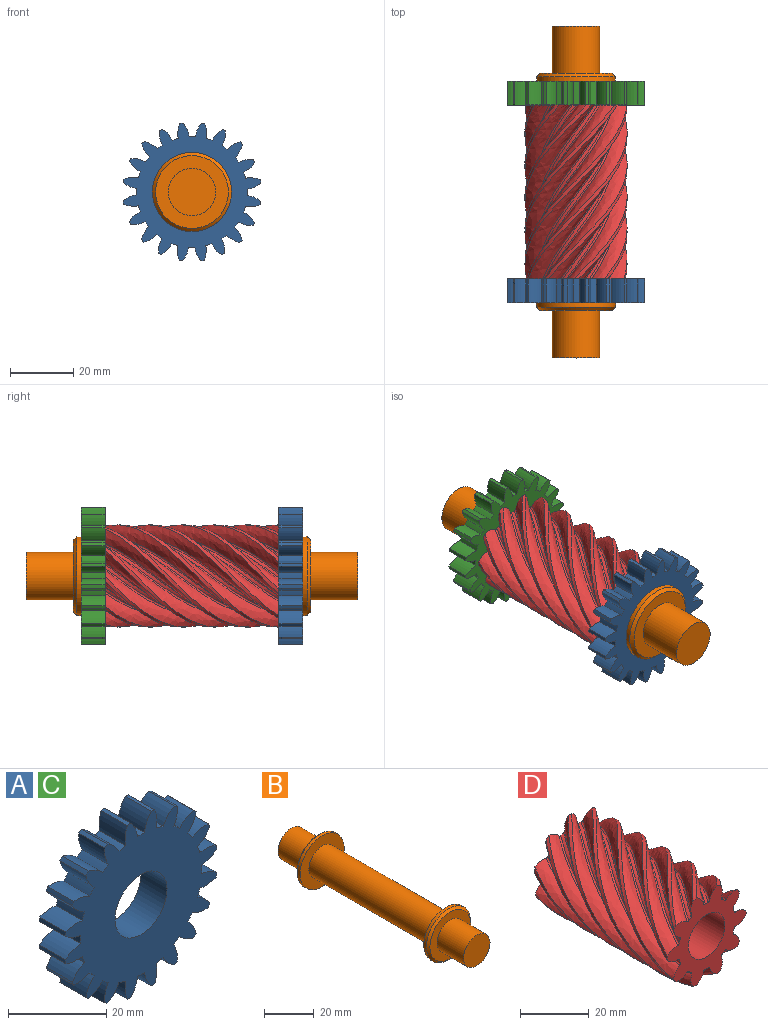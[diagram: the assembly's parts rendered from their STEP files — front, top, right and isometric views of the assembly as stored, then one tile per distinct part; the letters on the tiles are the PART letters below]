
ASSEMBLY  parts=4 mates=3
PART A: 83 faces, bbox 43.6x7.5x43.6 mm
  f0: cylinder r=22mm len=7.5mm, axis (0,-1,0), area 7.8mm2, adj f2,f76,f79,f80
  f1: cylinder r=8mm len=7.5mm, axis (0,-1,0), area 36.1mm2, adj f3,f4,f76,f79
  f2: cylinder r=8mm len=7.5mm, axis (0,-1,0), area 36.1mm2, adj f0,f3,f76,f79
  f3: cylinder r=17.5mm len=7.5mm, axis (0,-1,0), area 15mm2, adj f1,f2,f76,f79
  f4: cylinder r=22mm len=7.5mm, axis (0,-1,0), area 7.8mm2, adj f1,f6,f76,f79
  f5: cylinder r=8mm len=7.5mm, axis (0,-1,0), area 36.1mm2, adj f7,f8,f76,f79
  f6: cylinder r=8mm len=7.5mm, axis (0,-1,0), area 36.1mm2, adj f4,f7,f76,f79
  f7: cylinder r=17.5mm len=7.5mm, axis (0,-1,0), area 15mm2, adj f5,f6,f76,f79
  f8: cylinder r=22mm len=7.5mm, axis (0,-1,0), area 7.8mm2, adj f5,f10,f76,f79
  f9: cylinder r=8mm len=7.5mm, axis (0,-1,0), area 36.1mm2, adj f11,f12,f76,f79
  f10: cylinder r=8mm len=7.5mm, axis (0,-1,0), area 36.1mm2, adj f8,f11,f76,f79
  f11: cylinder r=17.5mm len=7.5mm, axis (0,-1,0), area 15mm2, adj f9,f10,f76,f79
  f12: cylinder r=22mm len=7.5mm, axis (0,-1,0), area 7.8mm2, adj f9,f14,f76,f79
  f13: cylinder r=8mm len=7.5mm, axis (0,-1,0), area 36.1mm2, adj f15,f16,f76,f79
  f14: cylinder r=8mm len=7.5mm, axis (0,-1,0), area 36.1mm2, adj f12,f15,f76,f79
  f15: cylinder r=17.5mm len=7.5mm, axis (0,-1,0), area 15mm2, adj f13,f14,f76,f79
  f16: cylinder r=22mm len=7.5mm, axis (0,-1,0), area 7.8mm2, adj f13,f18,f76,f79
  f17: cylinder r=8mm len=7.5mm, axis (0,-1,0), area 36.1mm2, adj f19,f20,f76,f79
  f18: cylinder r=8mm len=7.5mm, axis (0,-1,0), area 36.1mm2, adj f16,f19,f76,f79
  f19: cylinder r=17.5mm len=7.5mm, axis (0,-1,0), area 15mm2, adj f17,f18,f76,f79
  f20: cylinder r=22mm len=7.5mm, axis (0,-1,0), area 7.8mm2, adj f17,f22,f76,f79
  f21: cylinder r=8mm len=7.5mm, axis (0,-1,0), area 36.1mm2, adj f23,f24,f76,f79
  f22: cylinder r=8mm len=7.5mm, axis (0,-1,0), area 36.1mm2, adj f20,f23,f76,f79
  f23: cylinder r=17.5mm len=7.5mm, axis (0,-1,0), area 15mm2, adj f21,f22,f76,f79
  f24: cylinder r=22mm len=7.5mm, axis (0,-1,0), area 7.8mm2, adj f21,f26,f76,f79
  f25: cylinder r=8mm len=7.5mm, axis (0,-1,0), area 36.1mm2, adj f27,f28,f76,f79
  f26: cylinder r=8mm len=7.5mm, axis (0,-1,0), area 36.1mm2, adj f24,f27,f76,f79
  f27: cylinder r=17.5mm len=7.5mm, axis (0,-1,0), area 15mm2, adj f25,f26,f76,f79
  f28: cylinder r=22mm len=7.5mm, axis (0,-1,0), area 7.8mm2, adj f25,f30,f76,f79
  f29: cylinder r=8mm len=7.5mm, axis (0,-1,0), area 36.1mm2, adj f31,f32,f76,f79
  f30: cylinder r=8mm len=7.5mm, axis (0,-1,0), area 36.1mm2, adj f28,f31,f76,f79
  f31: cylinder r=17.5mm len=7.5mm, axis (0,-1,0), area 15mm2, adj f29,f30,f76,f79
  f32: cylinder r=22mm len=7.5mm, axis (0,-1,0), area 7.8mm2, adj f29,f34,f76,f79
  f33: cylinder r=8mm len=7.5mm, axis (0,-1,0), area 36.1mm2, adj f35,f36,f76,f79
  f34: cylinder r=8mm len=7.5mm, axis (0,-1,0), area 36.1mm2, adj f32,f35,f76,f79
  f35: cylinder r=17.5mm len=7.5mm, axis (0,-1,0), area 15mm2, adj f33,f34,f76,f79
  f36: cylinder r=22mm len=7.5mm, axis (0,-1,0), area 7.8mm2, adj f33,f38,f76,f79
  f37: cylinder r=8mm len=7.5mm, axis (0,-1,0), area 36.1mm2, adj f39,f40,f76,f79
  f38: cylinder r=8mm len=7.5mm, axis (0,-1,0), area 36.1mm2, adj f36,f39,f76,f79
  f39: cylinder r=17.5mm len=7.5mm, axis (0,-1,0), area 15mm2, adj f37,f38,f76,f79
  f40: cylinder r=22mm len=7.5mm, axis (0,-1,0), area 7.8mm2, adj f37,f42,f76,f79
  f41: cylinder r=8mm len=7.5mm, axis (0,-1,0), area 36.1mm2, adj f43,f44,f76,f79
  f42: cylinder r=8mm len=7.5mm, axis (0,-1,0), area 36.1mm2, adj f40,f43,f76,f79
  f43: cylinder r=17.5mm len=7.5mm, axis (0,-1,0), area 15mm2, adj f41,f42,f76,f79
  f44: cylinder r=22mm len=7.5mm, axis (0,-1,0), area 7.8mm2, adj f41,f46,f76,f79
  f45: cylinder r=8mm len=7.5mm, axis (0,-1,0), area 36.1mm2, adj f47,f48,f76,f79
  f46: cylinder r=8mm len=7.5mm, axis (0,-1,0), area 36.1mm2, adj f44,f47,f76,f79
  f47: cylinder r=17.5mm len=7.5mm, axis (0,-1,0), area 15mm2, adj f45,f46,f76,f79
  f48: cylinder r=22mm len=7.5mm, axis (0,-1,0), area 7.8mm2, adj f45,f50,f76,f79
  f49: cylinder r=8mm len=7.5mm, axis (0,-1,0), area 36.1mm2, adj f51,f52,f76,f79
  f50: cylinder r=8mm len=7.5mm, axis (0,-1,0), area 36.1mm2, adj f48,f51,f76,f79
  f51: cylinder r=17.5mm len=7.5mm, axis (0,-1,0), area 15mm2, adj f49,f50,f76,f79
  f52: cylinder r=22mm len=7.5mm, axis (0,-1,0), area 7.8mm2, adj f49,f54,f76,f79
  f53: cylinder r=8mm len=7.5mm, axis (0,-1,0), area 36.1mm2, adj f55,f56,f76,f79
  f54: cylinder r=8mm len=7.5mm, axis (0,-1,0), area 36.1mm2, adj f52,f55,f76,f79
  f55: cylinder r=17.5mm len=7.5mm, axis (0,-1,0), area 15mm2, adj f53,f54,f76,f79
  f56: cylinder r=22mm len=7.5mm, axis (0,-1,0), area 7.8mm2, adj f53,f58,f76,f79
  f57: cylinder r=8mm len=7.5mm, axis (0,-1,0), area 36.1mm2, adj f59,f60,f76,f79
  f58: cylinder r=8mm len=7.5mm, axis (0,-1,0), area 36.1mm2, adj f56,f59,f76,f79
  f59: cylinder r=17.5mm len=7.5mm, axis (0,-1,0), area 15mm2, adj f57,f58,f76,f79
  f60: cylinder r=22mm len=7.5mm, axis (0,-1,0), area 7.8mm2, adj f57,f62,f76,f79
  f61: cylinder r=8mm len=7.5mm, axis (0,-1,0), area 36.1mm2, adj f63,f64,f76,f79
  f62: cylinder r=8mm len=7.5mm, axis (0,-1,0), area 36.1mm2, adj f60,f63,f76,f79
  f63: cylinder r=17.5mm len=7.5mm, axis (0,-1,0), area 15mm2, adj f61,f62,f76,f79
  f64: cylinder r=22mm len=7.5mm, axis (0,-1,0), area 7.8mm2, adj f61,f66,f76,f79
  f65: cylinder r=8mm len=7.5mm, axis (0,-1,0), area 36.1mm2, adj f67,f68,f76,f79
  f66: cylinder r=8mm len=7.5mm, axis (0,-1,0), area 36.1mm2, adj f64,f67,f76,f79
  f67: cylinder r=17.5mm len=7.5mm, axis (0,-1,0), area 15mm2, adj f65,f66,f76,f79
  f68: cylinder r=22mm len=7.5mm, axis (0,-1,0), area 7.8mm2, adj f65,f70,f76,f79
  f69: cylinder r=8mm len=7.5mm, axis (0,-1,0), area 36.1mm2, adj f71,f72,f76,f79
  f70: cylinder r=8mm len=7.5mm, axis (0,-1,0), area 36.1mm2, adj f68,f71,f76,f79
  f71: cylinder r=17.5mm len=7.5mm, axis (0,-1,0), area 15mm2, adj f69,f70,f76,f79
  f72: cylinder r=22mm len=7.5mm, axis (0,-1,0), area 7.8mm2, adj f69,f74,f76,f79
  f73: cylinder r=8mm len=7.5mm, axis (0,-1,0), area 36.1mm2, adj f75,f76,f78,f79
  f74: cylinder r=8mm len=7.5mm, axis (0,-1,0), area 36.1mm2, adj f72,f75,f76,f79
  f75: cylinder r=17.5mm len=7.5mm, axis (0,-1,0), area 15mm2, adj f73,f74,f76,f79
  f76: plane 43.61x43.61mm, normal (0,-1,0), area 1034.8mm2, adj f0,f1,f2,f3,f4,f5,f6,f7
  f77: cylinder r=7.5mm len=15mm, axis (0,-1,0), area 353.4mm2, adj f76,f79
  f78: cylinder r=22mm len=7.5mm, axis (0,-1,0), area 7.8mm2, adj f73,f76,f79,f81
  f79: plane 43.61x43.61mm, normal (0,1,0), area 1034.8mm2, adj f0,f1,f2,f3,f4,f5,f6,f7
  f80: cylinder r=8mm len=7.5mm, axis (0,-1,0), area 36.1mm2, adj f0,f76,f79,f82
  f81: cylinder r=8mm len=7.5mm, axis (0,-1,0), area 36.1mm2, adj f76,f78,f79,f82
  f82: cylinder r=17.5mm len=7.5mm, axis (0,-1,0), area 15mm2, adj f76,f79,f80,f81
PART B: 13 faces, bbox 25x105x25 mm
  f0: plane 15x15mm, normal (0,1,0), area 176.7mm2, adj f10
  f1: plane 15x15mm, normal (0,-1,0), area 176.7mm2, adj f2
  f2: cylinder r=7.5mm len=15mm, axis (0,-1,0), area 706.9mm2, adj f1,f3
  f3: plane 23x23mm, normal (0,-1,0), area 238.8mm2, adj f2,f12
  f4: cylinder r=12.5mm len=25mm, axis (0,-1,0), area 117.8mm2, adj f5,f12
  f5: plane 25x25mm, normal (0,1,0), area 314.2mm2, adj f4,f6
  f6: cylinder r=7.5mm len=70mm, axis (0,-1,0), area 3298.7mm2, adj f5,f7
  f7: plane 25x25mm, normal (0,-1,0), area 314.2mm2, adj f6,f8
  f8: cylinder r=12.5mm len=25mm, axis (0,-1,0), area 117.8mm2, adj f7,f11
  f9: plane 23x23mm, normal (0,1,0), area 238.8mm2, adj f10,f11
  f10: cylinder r=7.5mm len=15mm, axis (0,-1,0), area 706.9mm2, adj f0,f9
  f11: cone r=12.5mm half-angle=45deg, axis (0,-1,0), area 106.6mm2, adj f8,f9
  f12: cone r=11.5mm half-angle=45deg, axis (0,1,0), area 106.6mm2, adj f3,f4
PART C: same geometry as A
PART D: 63 faces, bbox 33.1x59.2x33.1 mm
  f0: cylinder r=11.65mm len=55mm, axis (0,-1,0), area 68.8mm2, adj f11,f12,f44,f62
  f1: cylinder r=11.65mm len=55mm, axis (0,-1,0), area 68.8mm2, adj f11,f12,f43,f46
  f2: cylinder r=11.65mm len=55mm, axis (0,-1,0), area 68.8mm2, adj f11,f12,f45,f48
  f3: cylinder r=11.65mm len=55mm, axis (0,-1,0), area 68.8mm2, adj f11,f12,f47,f50
  f4: cylinder r=11.65mm len=55mm, axis (0,-1,0), area 68.8mm2, adj f11,f12,f49,f52
  f5: cylinder r=11.65mm len=55mm, axis (0,-1,0), area 68.8mm2, adj f11,f12,f53,f56
  f6: cylinder r=11.65mm len=55mm, axis (0,-1,0), area 68.8mm2, adj f11,f12,f55,f58
  f7: cylinder r=11.65mm len=55mm, axis (0,-1,0), area 68.8mm2, adj f11,f12,f51,f54
  f8: cylinder r=11.65mm len=55mm, axis (0,-1,0), area 68.8mm2, adj f11,f12,f57,f60
  f9: cylinder r=11.65mm len=55mm, axis (0,-1,0), area 68.8mm2, adj f11,f12,f59,f61
  f10: cylinder r=7.5mm len=55mm, axis (0,-1,0), area 2591.8mm2, adj f11,f12
  f11: plane 32.41x31.74mm, normal (0,1,0), area 440.6mm2, adj f0,f1,f2,f3,f4,f5,f6,f7
  f12: plane 32.42x31.27mm, normal (0,-1,0), area 440.6mm2, adj f0,f1,f2,f3,f4,f5,f6,f7
  f13: bspline ~57.29x32.56mm, area 82.5mm2, adj f11,f12,f14,f15
  f14: bspline ~57.29x32.41mm, area 329.3mm2, adj f11,f12,f13,f62
  f15: bspline ~57.29x32.56mm, area 329.3mm2, adj f11,f12,f13,f61
  f16: bspline ~57.29x32.33mm, area 82.5mm2, adj f11,f12,f17,f18
  f17: bspline ~55x31.42mm, area 329.3mm2, adj f11,f12,f16,f59
  f18: bspline ~57.29x31.92mm, area 329.3mm2, adj f11,f12,f16,f60
  f19: bspline ~57.29x30.62mm, area 82.5mm2, adj f11,f12,f20,f21
  f20: bspline ~57.29x30.55mm, area 329.3mm2, adj f11,f12,f19,f53
  f21: bspline ~57.29x29.96mm, area 329.3mm2, adj f11,f12,f19,f54
  f22: bspline ~57.29x32mm, area 82.5mm2, adj f11,f12,f23,f24
  f23: bspline ~57.29x31.36mm, area 329.3mm2, adj f11,f12,f22,f57
  f24: bspline ~57.29x32mm, area 329.3mm2, adj f11,f12,f22,f58
  f25: bspline ~55x32.3mm, area 82.5mm2, adj f11,f12,f26,f27
  f26: bspline ~57.29x32.85mm, area 329.3mm2, adj f11,f12,f25,f55
  f27: bspline ~55x32.2mm, area 329.3mm2, adj f11,f12,f25,f56
  f28: bspline ~57.29x32.56mm, area 82.5mm2, adj f11,f12,f29,f30
  f29: bspline ~57.29x32.41mm, area 329.3mm2, adj f11,f12,f28,f51
  f30: bspline ~57.29x32.56mm, area 329.3mm2, adj f11,f12,f28,f52
  f31: bspline ~57.29x32.33mm, area 82.5mm2, adj f11,f12,f32,f33
  f32: bspline ~55x31.42mm, area 329.3mm2, adj f11,f12,f31,f49
  f33: bspline ~57.29x31.92mm, area 329.3mm2, adj f11,f12,f31,f50
  f34: bspline ~57.29x32mm, area 82.5mm2, adj f11,f12,f35,f36
  f35: bspline ~57.29x31.36mm, area 329.3mm2, adj f11,f12,f34,f47
  f36: bspline ~57.29x32mm, area 329.3mm2, adj f11,f12,f34,f48
  f37: bspline ~55x32.3mm, area 82.5mm2, adj f11,f12,f38,f39
  f38: bspline ~57.29x32.85mm, area 329.3mm2, adj f11,f12,f37,f45
  f39: bspline ~55x32.2mm, area 329.3mm2, adj f11,f12,f37,f46
  f40: bspline ~57.29x30.62mm, area 82.5mm2, adj f11,f12,f41,f42
  f41: bspline ~57.29x30.55mm, area 329.3mm2, adj f11,f12,f40,f43
  f42: bspline ~57.29x29.96mm, area 329.3mm2, adj f11,f12,f40,f44
  f43: bspline ~58.6x23.38mm, area 49.4mm2, adj f1,f11,f12,f41
  f44: bspline ~57.55x23.56mm, area 49.4mm2, adj f0,f11,f12,f42
  f45: bspline ~58.6x24.21mm, area 49.4mm2, adj f2,f11,f12,f38
  f46: bspline ~57.55x23.9mm, area 49.4mm2, adj f1,f11,f12,f39
  f47: bspline ~58.6x23.11mm, area 49.4mm2, adj f3,f11,f12,f35
  f48: bspline ~57.55x24.21mm, area 49.4mm2, adj f2,f11,f12,f36
  f49: bspline ~58.6x24.18mm, area 49.4mm2, adj f4,f11,f12,f32
  f50: bspline ~57.55x22.48mm, area 49.4mm2, adj f3,f11,f12,f33
  f51: bspline ~58.6x24.12mm, area 49.4mm2, adj f7,f11,f12,f29
  f52: bspline ~57.55x24.21mm, area 49.4mm2, adj f4,f11,f12,f30
  f53: bspline ~58.6x23.38mm, area 49.4mm2, adj f5,f11,f12,f20
  f54: bspline ~57.55x23.56mm, area 49.4mm2, adj f7,f11,f12,f21
  f55: bspline ~58.6x24.21mm, area 49.4mm2, adj f6,f11,f12,f26
  f56: bspline ~57.55x23.9mm, area 49.4mm2, adj f5,f11,f12,f27
  f57: bspline ~58.6x23.11mm, area 49.4mm2, adj f8,f11,f12,f23
  f58: bspline ~57.55x24.21mm, area 49.4mm2, adj f6,f11,f12,f24
  f59: bspline ~58.6x24.18mm, area 49.4mm2, adj f9,f11,f12,f17
  f60: bspline ~57.55x22.48mm, area 49.4mm2, adj f8,f11,f12,f18
  f61: bspline ~57.55x24.21mm, area 49.4mm2, adj f9,f11,f12,f15
  f62: bspline ~58.6x24.12mm, area 49.4mm2, adj f0,f11,f12,f14
PLACE A rot(axis=(0,1,0),18.3deg) t=(80.37,-5.4,-49.66)mm
PLACE B t=(80.37,29.6,-49.66)mm
PLACE C rot(axis=(0,1,0),18.3deg) t=(80.37,57.1,-49.66)mm
PLACE D rot(axis=(0,-1,0),161.7deg) t=(80.37,2.1,-49.66)mm
MATE fastened A.f77 <-> D.f10  axis (0,-1,0) through (80.37,2.1,-49.66)mm
MATE fastened C.f77 <-> D.f10  axis (0,-1,0) through (80.37,57.1,-49.66)mm
MATE revolute D.f10 <-> B.f2  axis (0,-1,0) through (80.37,29.6,-49.66)mm
